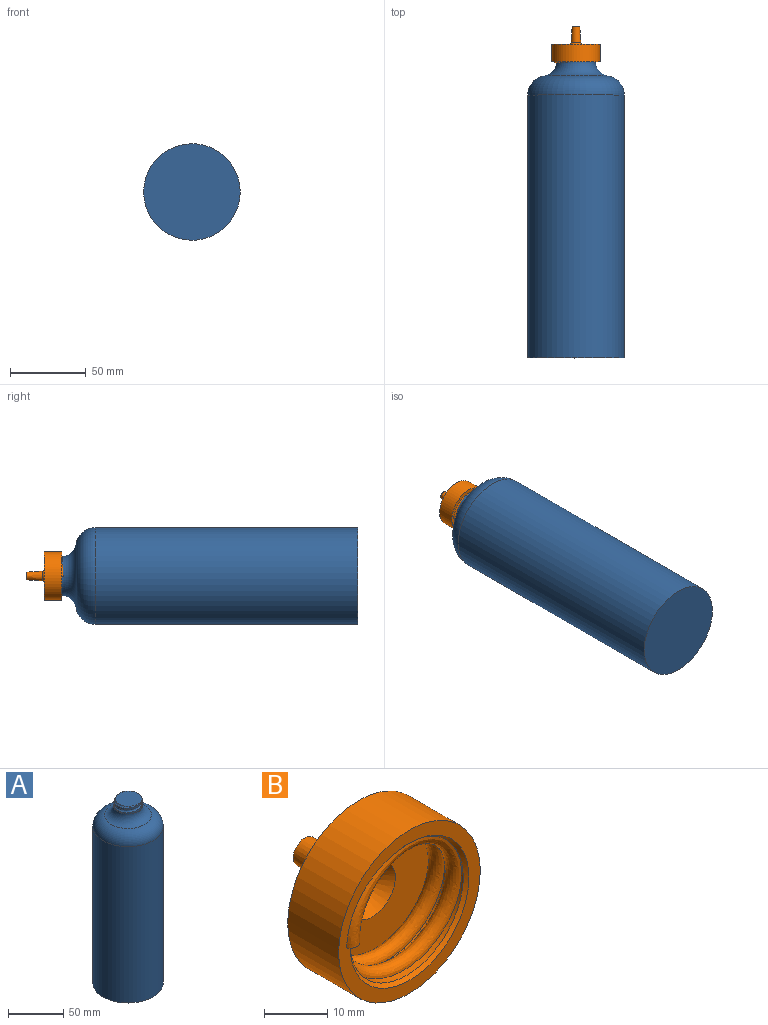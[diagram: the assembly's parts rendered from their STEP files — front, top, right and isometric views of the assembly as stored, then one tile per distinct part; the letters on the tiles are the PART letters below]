
ASSEMBLY  parts=2 mates=1
PART A: 8 faces, bbox 75.1x75.1x212.7 mm
  f0: cylinder r=12.7mm len=25.4mm, axis (0,0,1), area 225.3mm2, adj f1,f3,f7
  f1: bspline ~25.36x25.31mm, area 86.4mm2, adj f0,f2,f7
  f2: plane 31.75x25.05mm, normal (0,0,1), area 59.2mm2, adj f1,f3
  f3: torus R=22.86mm, axis (0,0,1), area 1408.4mm2, adj f0,f2,f5
  f4: cylinder r=31.75mm len=173.04mm, axis (0,0,1), area 34519.9mm2, adj f5,f6
  f5: torus R=19.05mm, axis (0,0,1), area 3132.5mm2, adj f3,f4
  f6: plane 63.5x63.5mm, normal (0,0,-1), area 3166.9mm2, adj f4
  f7: plane 25.53x25.32mm, normal (0,0,1), area 447.6mm2, adj f0,f1
PART B: 13 faces, bbox 32.8x25.5x32.8 mm
  f0: plane 32.19x32.19mm, normal (0,-1,0), area 225.2mm2, adj f2,f3,f10,f12
  f1: cylinder r=12.7mm len=25.4mm, axis (0,1,0), area 170.3mm2, adj f2,f9,f10,f11,f12
  f2: cone r=1.91mm half-angle=45deg, axis (0,-1,0), area 51.5mm2, adj f0,f1,f10,f12
  f3: cylinder r=15.88mm len=31.75mm, axis (0,1,0), area 1140.1mm2, adj f0,f4
  f4: plane 31.75x31.75mm, normal (0,1,0), area 722.9mm2, adj f3,f7
  f5: cone r=3.17mm half-angle=3deg, axis (0,-1,0), area 188.2mm2, adj f6,f7
  f6: cone r=1.91mm half-angle=3deg, axis (0,1,0), area 169.4mm2, adj f5,f8
  f7: torus R=4.68mm, axis (0,-1,0), area 55.9mm2, adj f4,f5
  f8: cone r=1.91mm half-angle=45deg, axis (0,-1,0), area 98.5mm2, adj f6,f9
  f9: plane 26.42x25.25mm, normal (0,-1,0), area 389.3mm2, adj f1,f8,f11,f12
  f10: plane 3.71x3.57mm, normal (0,0,-1), area 4.7mm2, adj f0,f1,f2,f12
  f11: plane 1.96x1.96mm, normal (0,0,1), area 1.8mm2, adj f1,f9,f12
  f12: bspline ~28.16x28.14mm, area 691.6mm2, adj f0,f1,f2,f9,f10,f11
PLACE A rot(axis=(-1,0,0),90deg) t=(0,-76.2,0)mm
PLACE B at identity
MATE cylindrical B.f1 <-> A.f0  axis (0,1,0) through (0,-3.81,0)mm
